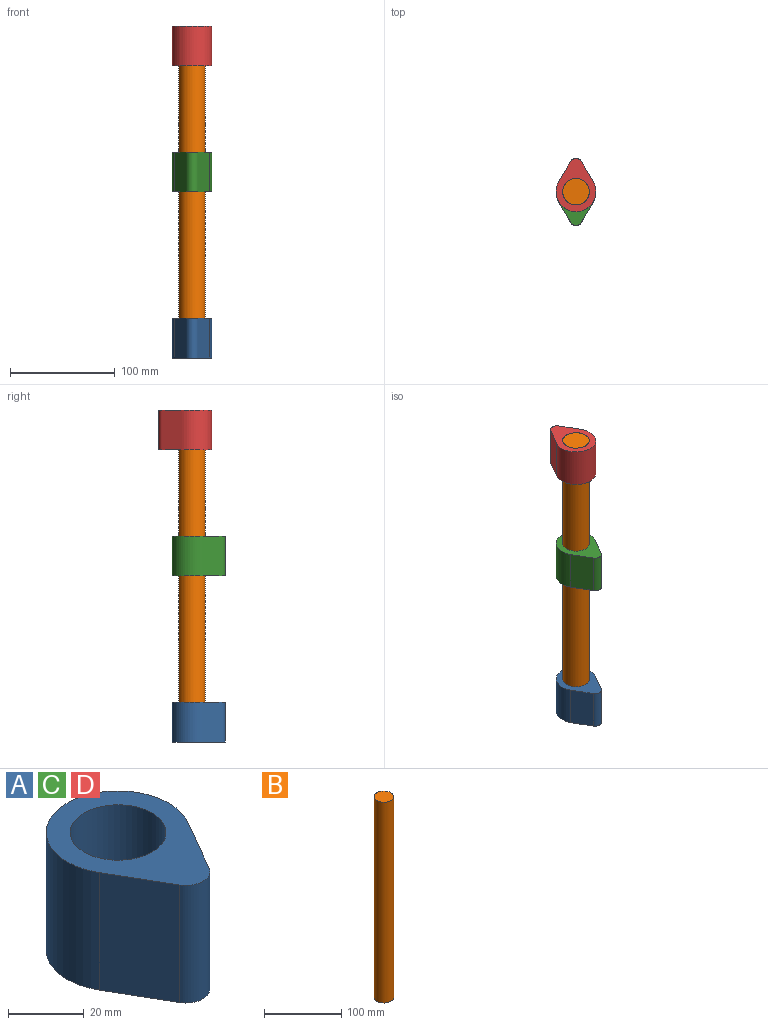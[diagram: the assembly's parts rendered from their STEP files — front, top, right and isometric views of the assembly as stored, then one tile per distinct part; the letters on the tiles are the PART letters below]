
ASSEMBLY  parts=4 mates=2
PART A: 7 faces, bbox 38.1x50.8x38.1 mm
  f0: plane 38.1x19.05mm, normal (-0.87,-0.5,0), area 838.1mm2, adj f1,f4,f5,f6
  f1: cylinder r=6.35mm len=38.1mm, axis (0,0,-1), area 506.7mm2, adj f0,f2,f5,f6
  f2: plane 38.1x19.05mm, normal (0.87,-0.5,0), area 838.1mm2, adj f1,f4,f5,f6
  f3: cylinder r=12.7mm len=38.1mm, axis (0,0,-1), area 3040.2mm2, adj f5,f6
  f4: cylinder r=19.05mm len=38.1mm, axis (0,0,-1), area 3040.2mm2, adj f0,f2,f5,f6
  f5: plane 50.8x38.1mm, normal (0,0,1), area 854.3mm2, adj f0,f1,f2,f3,f4
  f6: plane 50.8x38.1mm, normal (0,0,-1), area 854.3mm2, adj f0,f1,f2,f3,f4
PART B: 3 faces, bbox 25.4x25.4x317.5 mm
  f0: cylinder r=12.7mm len=317.5mm, axis (0,0,-1), area 25335.4mm2, adj f1,f2
  f1: plane 25.4x25.4mm, normal (0,0,1), area 506.7mm2, adj f0
  f2: plane 25.4x25.4mm, normal (0,0,-1), area 506.7mm2, adj f0
PART C: same geometry as A
PART D: same geometry as A
PLACE A at identity
PLACE B at identity
PLACE C t=(0,0,158.75)mm
PLACE D rot(axis=(0,0,1),180deg) t=(0,0,279.4)mm
MATE planar D.f3 <-> B.f0  axis (0,0,-1) through (0,0,317.5)mm
MATE planar C.f3 <-> B.f0  axis (0,0,-1) through (0,0,158.75)mm
